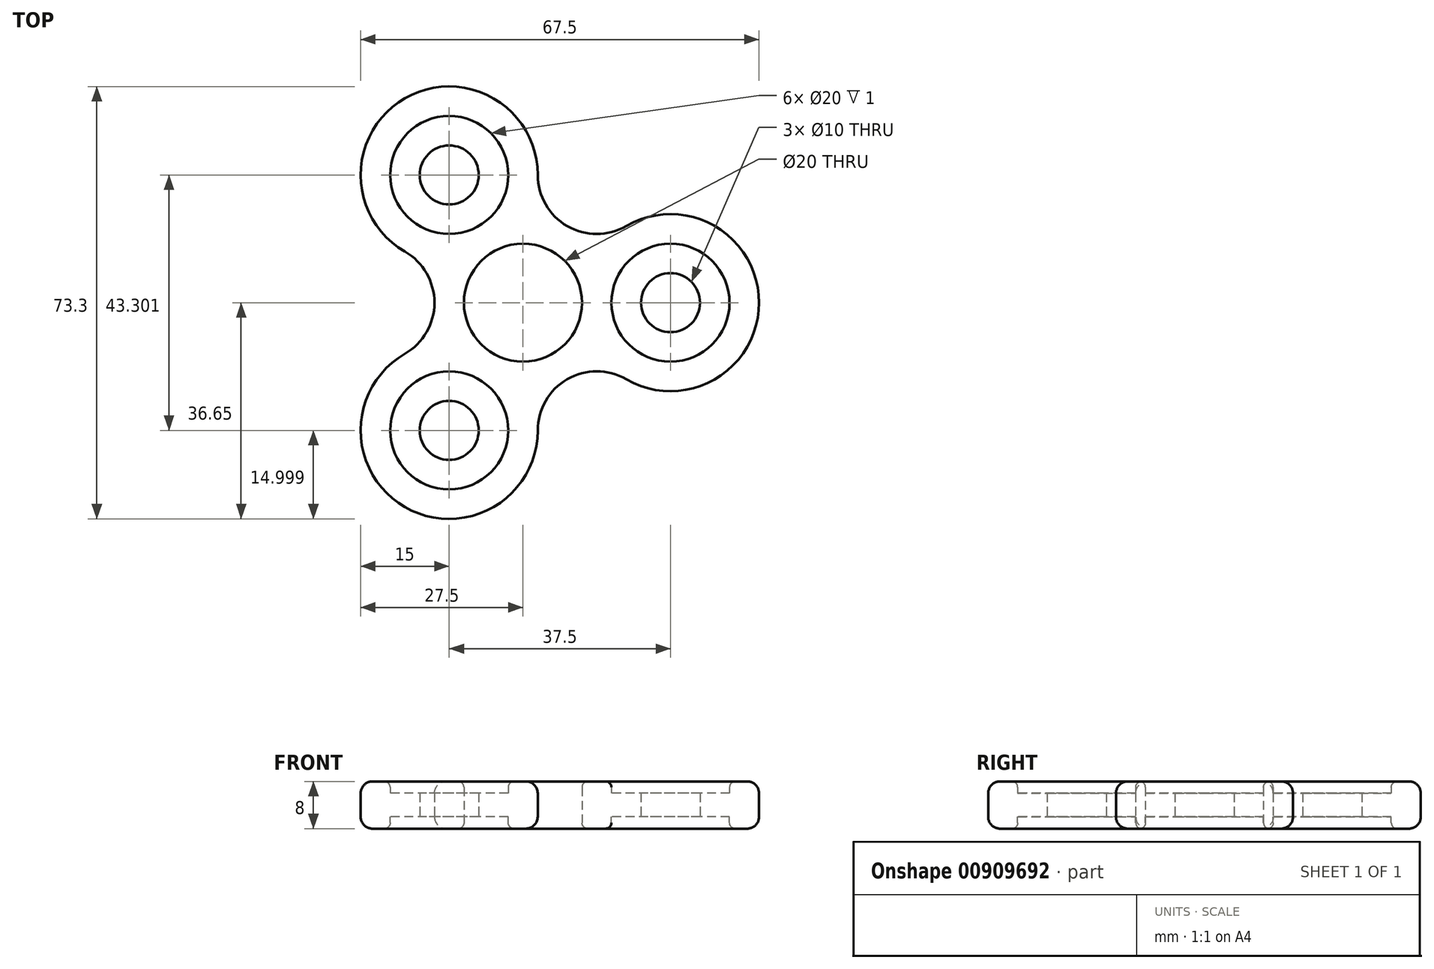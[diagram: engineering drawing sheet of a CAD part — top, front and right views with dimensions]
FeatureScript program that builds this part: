
annotation { "Feature Type Name" : "Feature", "Feature Type Description" : "" }
export const myFeature = defineFeature(function(context is Context, id is Id, definition is map)
    precondition{}
    {
        {
            var Q0;
            Q0=qCreatedBy(makeId("Top.planeOp"),FACE);
            var sketch = newSketch(context, id + "F0", { "sketchPlane" : qUnion([Q0])});
            skCircle(sketch, "E0", {"center": v(0, 0) * mm, "radius": 10 * mm});
            skCircle(sketch, "E1", {"center": v(25, 0) * mm, "radius": 10 * mm});
            skCircle(sketch, "E2", {"center": v(0, 0) * mm, "radius": 5 * mm});
            skCircle(sketch, "E3", {"center": v(25, 0) * mm, "radius": 5 * mm});
            skArc(sketch, "E4", {"start": v(17.5, -13) * mm, "mid": v(40, 0) * mm, "end": v(17.5, 13) * mm});
            skLineSegment(sketch, "E5", {"start": v(7.5, 13) * mm, "end": v(7.5, 13) * mm});
            skPoint(sketch, "E6", {"position": v(12.5, 8.3) * mm});
            skPoint(sketch, "E7", {"position": v(12.5, -8.3) * mm});
            skArc(sketch, "E8.1.0", {"start": v(2.5, 21.65) * mm, "mid": v(-20, 34.64) * mm, "end": v(-20, 8.66) * mm});
            skCircle(sketch, "E8.1.1", {"center": v(-12.5, 21.65) * mm, "radius": 10 * mm});
            skPoint(sketch, "E8.1.2", {"position": v(-13.43, 6.68) * mm});
            skCircle(sketch, "E8.1.3", {"center": v(-12.5, 21.65) * mm, "radius": 5 * mm});
            skPoint(sketch, "E8.1.4", {"position": v(0.93, 14.97) * mm});
            skArc(sketch, "E8.2.0", {"start": v(-20, -8.66) * mm, "mid": v(-20, -34.64) * mm, "end": v(2.5, -21.65) * mm});
            skCircle(sketch, "E8.2.1", {"center": v(-12.5, -21.65) * mm, "radius": 10 * mm});
            skPoint(sketch, "E8.2.2", {"position": v(0.93, -14.97) * mm});
            skCircle(sketch, "E8.2.3", {"center": v(-12.5, -21.65) * mm, "radius": 5 * mm});
            skPoint(sketch, "E8.2.4", {"position": v(-13.43, -6.68) * mm});
            skLineSegment(sketch, "E9.trimOffspring", {"start": v(-15, 0) * mm, "end": v(-15, 0) * mm});
            skLineSegment(sketch, "E10.trimOffspring", {"start": v(7.5, -13) * mm, "end": v(7.5, -13) * mm});
            skArc(sketch, "E11.filletArc", {"start": v(2.5, 21.65) * mm, "mid": v(3.84, 16.65) * mm, "end": v(7.5, 13) * mm});
            skArc(sketch, "E12.filletArc", {"start": v(7.5, 13) * mm, "mid": v(12.5, 11.65) * mm, "end": v(17.5, 13) * mm});
            skArc(sketch, "E13.filletArc", {"start": v(17.5, -13) * mm, "mid": v(12.5, -11.65) * mm, "end": v(7.5, -13) * mm});
            skArc(sketch, "E14.filletArc", {"start": v(7.5, -13) * mm, "mid": v(3.84, -16.65) * mm, "end": v(2.5, -21.65) * mm});
            skArc(sketch, "E15.filletArc", {"start": v(-20, -8.66) * mm, "mid": v(-16.34, -5) * mm, "end": v(-15, 0) * mm});
            skArc(sketch, "E16.filletArc", {"start": v(-15, 0) * mm, "mid": v(-16.34, 5) * mm, "end": v(-20, 8.66) * mm});
            skSolve(sketch);
        }
        {
            var Q0;
            Q0 = qSketchRegion(id + "F0", true);
            extrude(context, id + "F1", {"entities" : qUnion([Q0]), "depth" : 4 * mm, "offsetDistance" : 25 * mm});
        }
        {
            var Q0;
            Q0=makeQuery(id+"F0.imprint","IMPRINT",FACE,{"disambiguationData":[TD([[makeQuery(id+"F0.imprint","IMPRINT",EDGE,{"derivedFrom":sQuery(id+"F0.wireOp",EDGE,"E8.1.1")}),1.0]])]});
            var Q1;
            Q1=makeQuery(id+"F0.imprint","IMPRINT",FACE,{"disambiguationData":[TD([[makeQuery(id+"F0.imprint","IMPRINT",EDGE,{"derivedFrom":sQuery(id+"F0.wireOp",EDGE,"E1")}),1.0]])]});
            var Q2;
            Q2=makeQuery(id+"F0.imprint","IMPRINT",FACE,{"disambiguationData":[TD([[makeQuery(id+"F0.imprint","IMPRINT",EDGE,{"derivedFrom":sQuery(id+"F0.wireOp",EDGE,"E8.2.1")}),1.0]])]});
            extrude(context, id + "F2", {"entities" : qUnion([Q0, Q1, Q2]), "operationType" : NewBodyOperationType.ADD, "depth" : 2 * mm, "offsetDistance" : 25 * mm});
        }
        {
            var Q0;
            Q0=makeQuery(id+"F1.opExtrude","CAP_EDGE",EDGE,{"disambiguationData":[OSD([sQuery(id+"F0.wireOp",EDGE,"E8.1.1")])],"isStart":false});
            var Q1;
            Q1=makeQuery(id+"F1.opExtrude","CAP_EDGE",EDGE,{"disambiguationData":[OSD([sQuery(id+"F0.wireOp",EDGE,"E0")])],"isStart":false});
            var Q2;
            Q2=makeQuery(id+"F1.opExtrude","CAP_EDGE",EDGE,{"disambiguationData":[OSD([sQuery(id+"F0.wireOp",EDGE,"E1")])],"isStart":false});
            var Q3;
            Q3=makeQuery(id+"F1.opExtrude","CAP_EDGE",EDGE,{"disambiguationData":[OSD([sQuery(id+"F0.wireOp",EDGE,"E8.2.1")])],"isStart":false});
            fillet(context, id + "F3", {"entities" : qUnion([Q0, Q1, Q2, Q3]), "radius" : 1 * mm, "tangentPropagation" : true, "allowEdgeOverflow" : false});
        }
        {
            var Q0;
            Q0=makeQuery(id+"F1.opExtrude","CAP_EDGE",EDGE,{"disambiguationData":[OSD([sQuery(id+"F0.wireOp",EDGE,"E11.filletArc"),sQuery(id+"F0.wireOp",EDGE,"E12.filletArc")])],"isStart":false});
            var Q1;
            Q1=makeQuery(id+"F1.opExtrude","CAP_EDGE",EDGE,{"disambiguationData":[OSD([sQuery(id+"F0.wireOp",EDGE,"E8.1.0")])],"isStart":false});
            var Q2;
            Q2=makeQuery(id+"F1.opExtrude","CAP_EDGE",EDGE,{"disambiguationData":[OSD([sQuery(id+"F0.wireOp",EDGE,"E15.filletArc"),sQuery(id+"F0.wireOp",EDGE,"E16.filletArc")])],"isStart":false});
            var Q3;
            Q3=makeQuery(id+"F1.opExtrude","CAP_EDGE",EDGE,{"disambiguationData":[OSD([sQuery(id+"F0.wireOp",EDGE,"E8.2.0")])],"isStart":false});
            var Q4;
            Q4=makeQuery(id+"F1.opExtrude","CAP_EDGE",EDGE,{"disambiguationData":[OSD([sQuery(id+"F0.wireOp",EDGE,"E13.filletArc"),sQuery(id+"F0.wireOp",EDGE,"E14.filletArc")])],"isStart":false});
            var Q5;
            Q5=makeQuery(id+"F1.opExtrude","CAP_EDGE",EDGE,{"disambiguationData":[OSD([sQuery(id+"F0.wireOp",EDGE,"E4")])],"isStart":false});
            fillet(context, id + "F4", {"entities" : qUnion([Q0, Q1, Q2, Q3, Q4, Q5]), "radius" : 2 * mm, "tangentPropagation" : true, "allowEdgeOverflow" : false});
        }
        {
            var Q0;
            Q0=makeQuery(id+"F1.opExtrude","SWEPT_BODY",BODY,{"disambiguationData":[OSD([sQuery(id+"F0.wireOp",EDGE,"E0"),sQuery(id+"F0.wireOp",EDGE,"E1"),sQuery(id+"F0.wireOp",EDGE,"E4"),sQuery(id+"F0.wireOp",EDGE,"E8.1.0"),sQuery(id+"F0.wireOp",EDGE,"E8.1.1"),sQuery(id+"F0.wireOp",EDGE,"E8.2.0"),sQuery(id+"F0.wireOp",EDGE,"E8.2.1"),sQuery(id+"F0.wireOp",EDGE,"E11.filletArc"),sQuery(id+"F0.wireOp",EDGE,"E12.filletArc"),sQuery(id+"F0.wireOp",EDGE,"E13.filletArc"),sQuery(id+"F0.wireOp",EDGE,"E14.filletArc"),sQuery(id+"F0.wireOp",EDGE,"E15.filletArc"),sQuery(id+"F0.wireOp",EDGE,"E16.filletArc")])]});
            var Q1;
            Q1=qCreatedBy(makeId("Top.planeOp"),FACE);
            mirror(context, id + "F5", {"operationType" : NewBodyOperationType.ADD, "entities" : qUnion([Q0]), "mirrorPlane" : qUnion([Q1])});
        }
    });
